# Revit family: Allco COLD 288-125
name_source: partatom
category: Mechanical Equipment
units: mm (PartAtom-declared; Revit-internal decimal feet)

## family parameters
Always vertical = Yes
Classification = None
Cut with Voids When Loaded = Yes
Part Type = Normal
Room Calculation Point = No
Round Connector Dimension = Use Radius
Shared = No
Work Plane-Based = No

## types (6) — shared parameters
Diametr Opening = 11 mm  [stored 0.0360892 ft]
Material grille and ptorile = Aluminum
Material wanne = Galvanized coating
URL = www.allco-ag.ch

## per-type parameters (varying)
| type | Abstand 1 | Abstand 2 | Abstand 3 | Length | Openings |
| COLD 288-125 1130 mm | 827 mm  [stored 2.71325 ft] | 0 mm  [stored 0 ft] | 0 mm  [stored 0 ft] | 1130 mm  [stored 3.70735 ft] | Opening : L=1130 |
| COLD 288-125 1430 mm | 1127 mm  [stored 3.69751 ft] | 0 mm  [stored 0 ft] | 0 mm  [stored 0 ft] | 1430 mm  [stored 4.6916 ft] | Opening : L=1430 |
| COLD 288-125 1910 mm | 1028 mm  [stored 3.3727 ft] | 579 mm  [stored 1.89961 ft] | 0 mm  [stored 0 ft] | 1910 mm  [stored 6.2664 ft] | Opening : L=1910 |
| COLD 288-125 2210 mm | 1028 mm  [stored 3.3727 ft] | 879 mm  [stored 2.88386 ft] | 0 mm  [stored 0 ft] | 2210 mm  [stored 7.25066 ft] | Opening : L=2210 |
| COLD 288-125 2690 mm | 1028 mm  [stored 3.3727 ft] | 782 mm | 578 mm  [stored 1.89633 ft] | 2690 mm | Opening : L=2690 |
| COLD 288-125 2990 mm | 1028 mm  [stored 3.3727 ft] | 782 mm | 878 mm  [stored 2.88058 ft] | 2990 mm | Opening : L=2990 |

note: [stored X ft] marks values corroborated as IEEE doubles in the binary element streams (Revit-internal decimal feet)

## geometry (parser evidence)
native form markers: Blend x8, Sweep x14
no freeform markers — native parametric forms only
